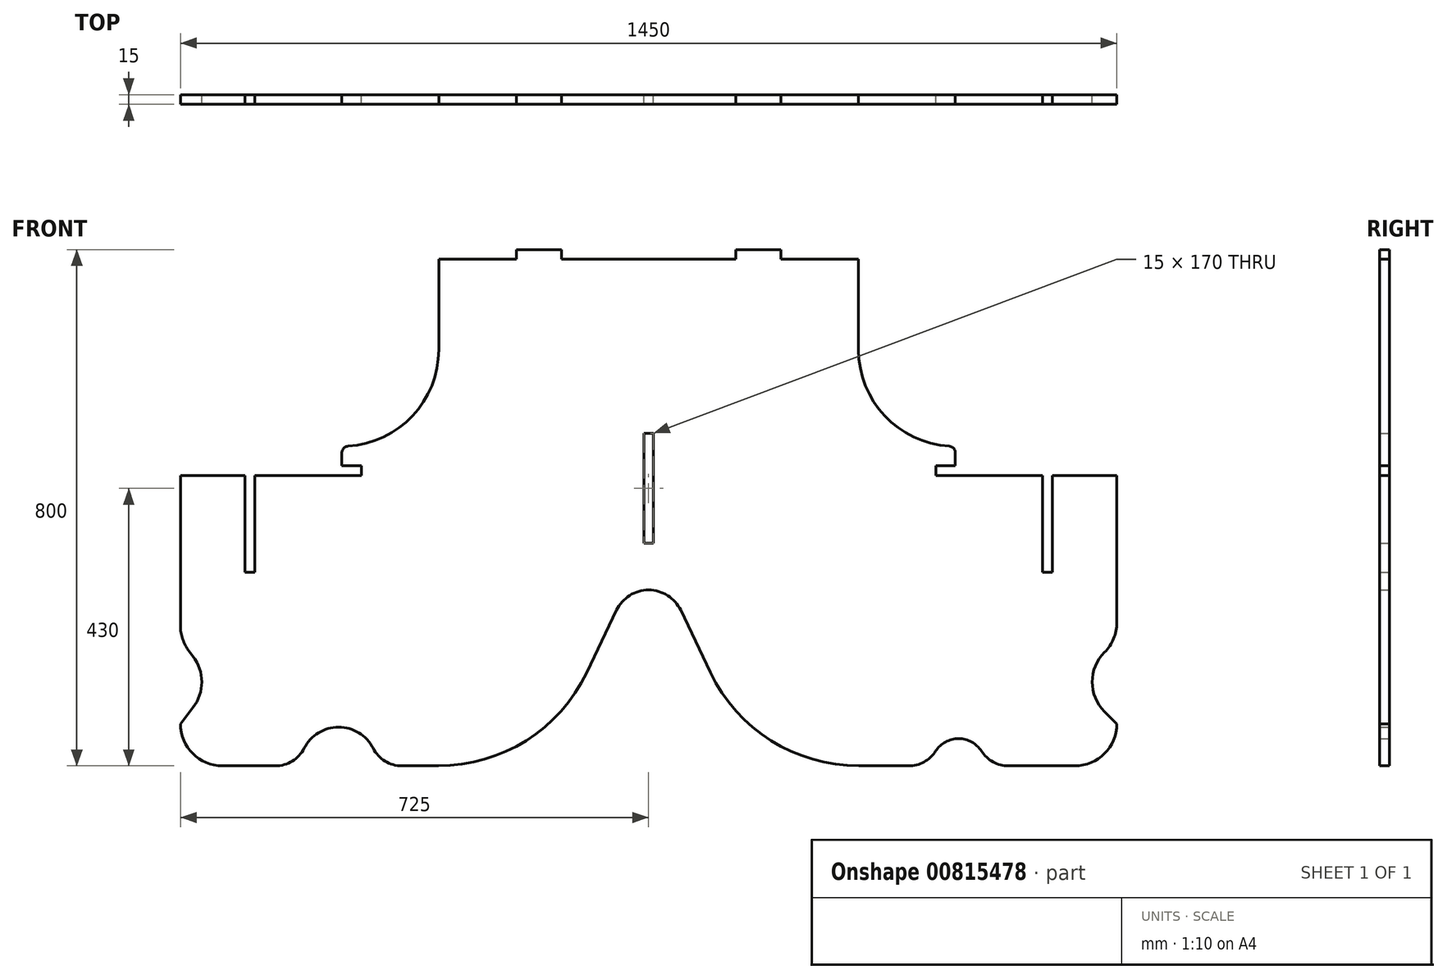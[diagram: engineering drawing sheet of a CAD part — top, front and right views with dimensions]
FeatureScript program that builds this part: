
annotation { "Feature Type Name" : "Feature", "Feature Type Description" : "" }
export const myFeature = defineFeature(function(context is Context, id is Id, definition is map)
    precondition{}
    {
        {
            var Q0;
            Q0=qCreatedBy(makeId("Front.planeOp"),FACE);
            var sketch = newSketch(context, id + "F0", { "sketchPlane" : qUnion([Q0])});
            skLineSegment(sketch, "E0.left", {"start": v(-325, 392.5) * mm, "end": v(-325, 312.5) * mm});
            skLineSegment(sketch, "E0.right", {"start": v(325, 392.5) * mm, "end": v(325, 312.5) * mm});
            skPoint(sketch, "E0.middle", {"position": v(0, 0) * mm});
            skLineSegment(sketch, "E1.bottom", {"start": v(-325, -392.5) * mm, "end": v(-382.02, -392.5) * mm});
            skLineSegment(sketch, "E2.bottom", {"start": v(325, -392.5) * mm, "end": v(402.54, -392.5) * mm});
            skLineSegment(sketch, "E3", {"start": v(-325, 392.5) * mm, "end": v(-205, 392.5) * mm});
            skLineSegment(sketch, "E4.top", {"start": v(-205, 407.5) * mm, "end": v(-135, 407.5) * mm});
            skLineSegment(sketch, "E4.left", {"start": v(-205, 392.5) * mm, "end": v(-205, 407.5) * mm});
            skLineSegment(sketch, "E4.right", {"start": v(-135, 392.5) * mm, "end": v(-135, 407.5) * mm});
            skLineSegment(sketch, "E5.top", {"start": v(205, 407.5) * mm, "end": v(135, 407.5) * mm});
            skLineSegment(sketch, "E5.left", {"start": v(205, 392.5) * mm, "end": v(205, 407.5) * mm});
            skLineSegment(sketch, "E5.right", {"start": v(135, 392.5) * mm, "end": v(135, 407.5) * mm});
            skLineSegment(sketch, "E6.trimOffspring", {"start": v(-135, 392.5) * mm, "end": v(135, 392.5) * mm});
            skLineSegment(sketch, "E7.trimOffspring", {"start": v(205, 392.5) * mm, "end": v(325, 392.5) * mm});
            skPoint(sketch, "E8.end.orphan", {"position": v(205, 374.36) * mm});
            skPoint(sketch, "E9.end.orphan", {"position": v(-205, 379.92) * mm});
            skLineSegment(sketch, "E10", {"start": v(0, -392.5) * mm, "end": v(0, -47.5) * mm});
            skLineSegment(sketch, "E11.right", {"start": v(-7.5, -47.5) * mm, "end": v(-7.5, 122.5) * mm});
            skLineSegment(sketch, "E12.MirrorCS", {"start": v(7.5, -47.5) * mm, "end": v(7.5, 122.5) * mm});
            skLineSegment(sketch, "E13", {"start": v(-7.5, 122.5) * mm, "end": v(7.5, 122.5) * mm});
            skLineSegment(sketch, "E14", {"start": v(-7.5, -47.5) * mm, "end": v(7.5, -47.5) * mm});
            skPoint(sketch, "E15.visualSharp", {"position": v(-146.32, -392.5) * mm});
            skPoint(sketch, "E16.visualSharp", {"position": v(165, -392.5) * mm});
            skLineSegment(sketch, "E17", {"start": v(-325.7, -392.5) * mm, "end": v(-325, -392.5) * mm});
            skLineSegment(sketch, "E18", {"start": v(325.7, -392.5) * mm, "end": v(325, -392.5) * mm});
            skLineSegment(sketch, "E19", {"start": v(-95.66, -247.52) * mm, "end": v(-49.62, -151.25) * mm});
            skLineSegment(sketch, "E20", {"start": v(49.62, -151.25) * mm, "end": v(95.66, -247.52) * mm});
            skPoint(sketch, "E21.visualSharp", {"position": v(0, -47.5) * mm});
            skArc(sketch, "E21.filletArc", {"start": v(49.62, -151.25) * mm, "mid": v(0, -119.98) * mm, "end": v(-49.62, -151.25) * mm});
            skPoint(sketch, "E22.visualSharp", {"position": v(-165, -392.5) * mm});
            skArc(sketch, "E22.filletArc", {"start": v(-325.7, -392.5) * mm, "mid": v(-189.75, -353.23) * mm, "end": v(-95.66, -247.52) * mm});
            skArc(sketch, "E23.filletArc", {"start": v(95.66, -247.52) * mm, "mid": v(189.75, -353.23) * mm, "end": v(325.7, -392.5) * mm});
            skLineSegment(sketch, "E24", {"start": v(-725, 57.5) * mm, "end": v(-625, 57.5) * mm});
            skLineSegment(sketch, "E25", {"start": v(-625, 57.5) * mm, "end": v(-625, -92.5) * mm});
            skLineSegment(sketch, "E26", {"start": v(-625, -92.5) * mm, "end": v(-610, -92.5) * mm});
            skLineSegment(sketch, "E27", {"start": v(-610, -92.5) * mm, "end": v(-610, 57.5) * mm});
            skLineSegment(sketch, "E28.trimOffspring", {"start": v(-625, 57.5) * mm, "end": v(-725, 57.5) * mm});
            skPoint(sketch, "E29.newPointA", {"position": v(-325, -392.5) * mm});
            skPoint(sketch, "E29.newPointB", {"position": v(-325, 57.5) * mm});
            skPoint(sketch, "E30.orphan", {"position": v(-525, 57.5) * mm});
            skPoint(sketch, "E31.newPointA", {"position": v(325, 57.5) * mm});
            skPoint(sketch, "E31.newPointB", {"position": v(325, -392.5) * mm});
            skLineSegment(sketch, "E32", {"start": v(725, 57.5) * mm, "end": v(625, 57.5) * mm});
            skLineSegment(sketch, "E33", {"start": v(625, 57.5) * mm, "end": v(625, -92.5) * mm});
            skLineSegment(sketch, "E34", {"start": v(625, -92.5) * mm, "end": v(610, -92.5) * mm});
            skLineSegment(sketch, "E35", {"start": v(610, -92.5) * mm, "end": v(610, 57.5) * mm});
            skLineSegment(sketch, "E36.trimOffspring", {"start": v(625, 57.5) * mm, "end": v(725, 57.5) * mm});
            skPoint(sketch, "E37.visualSharp", {"position": v(-725, -392.5) * mm});
            skArc(sketch, "E37.filletArc", {"start": v(-725, -327.5) * mm, "mid": v(-705.96, -373.46) * mm, "end": v(-660, -392.5) * mm});
            skPoint(sketch, "E38.visualSharp", {"position": v(725, -392.5) * mm});
            skArc(sketch, "E38.filletArc", {"start": v(660, -392.5) * mm, "mid": v(705.96, -373.46) * mm, "end": v(725, -327.5) * mm});
            skArc(sketch, "E39", {"start": v(515.45, -369.62) * mm, "mid": v(480, -350.3) * mm, "end": v(444.55, -369.62) * mm});
            skLineSegment(sketch, "E40.trimOffspring", {"start": v(557.46, -392.5) * mm, "end": v(660, -392.5) * mm});
            skPoint(sketch, "E41.visualSharp", {"position": v(437.8, -392.5) * mm});
            skArc(sketch, "E41.filletArc", {"start": v(402.54, -392.5) * mm, "mid": v(426.46, -386.4) * mm, "end": v(444.55, -369.62) * mm});
            skArc(sketch, "E42.filletArc", {"start": v(515.45, -369.62) * mm, "mid": v(533.54, -386.4) * mm, "end": v(557.46, -392.5) * mm});
            skArc(sketch, "E43", {"start": v(-426.56, -365.23) * mm, "mid": v(-480, -332.5) * mm, "end": v(-533.44, -365.23) * mm});
            skLineSegment(sketch, "E44.trimOffspring", {"start": v(-577.98, -392.5) * mm, "end": v(-660, -392.5) * mm});
            skPoint(sketch, "E45.visualSharp", {"position": v(-540, -392.5) * mm});
            skArc(sketch, "E45.filletArc", {"start": v(-577.98, -392.5) * mm, "mid": v(-551.87, -385.14) * mm, "end": v(-533.44, -365.23) * mm});
            skPoint(sketch, "E46.visualSharp", {"position": v(-420, -392.5) * mm});
            skArc(sketch, "E46.filletArc", {"start": v(-426.56, -365.23) * mm, "mid": v(-408.13, -385.14) * mm, "end": v(-382.02, -392.5) * mm});
            skLineSegment(sketch, "E47", {"start": v(525, 57.5) * mm, "end": v(525, 57.5) * mm});
            skLineSegment(sketch, "E48", {"start": v(325, 312.5) * mm, "end": v(325, 257.5) * mm});
            skLineSegment(sketch, "E49", {"start": v(-525, 57.5) * mm, "end": v(-525, 57.5) * mm});
            skLineSegment(sketch, "E50", {"start": v(-325, 312.5) * mm, "end": v(-325, 257.5) * mm});
            skLineSegment(sketch, "E51", {"start": v(-725, 57.5) * mm, "end": v(-725, -175.4) * mm});
            skLineSegment(sketch, "E52", {"start": v(-711.52, -215.02) * mm, "end": v(-705.49, -222.87) * mm});
            skLineSegment(sketch, "E53", {"start": v(-725, -327.5) * mm, "end": v(-705.49, -302.13) * mm});
            skPoint(sketch, "E54.visualSharp", {"position": v(-725, -197.5) * mm});
            skArc(sketch, "E54.filletArc", {"start": v(-725, -175.4) * mm, "mid": v(-721.54, -196.32) * mm, "end": v(-711.52, -215.02) * mm});
            skPoint(sketch, "E55.visualSharp", {"position": v(-675, -262.5) * mm});
            skArc(sketch, "E55.filletArc", {"start": v(-705.49, -302.13) * mm, "mid": v(-692, -262.5) * mm, "end": v(-705.49, -222.87) * mm});
            skLineSegment(sketch, "E56", {"start": v(705.96, -216.54) * mm, "end": v(705.96, -216.54) * mm});
            skLineSegment(sketch, "E57", {"start": v(705.96, -308.46) * mm, "end": v(725, -327.5) * mm});
            skLineSegment(sketch, "E58.trimOffspring", {"start": v(725, -170.58) * mm, "end": v(725, 57.5) * mm});
            skPoint(sketch, "E2.right.end.orphan", {"position": v(725, -262.5) * mm});
            skPoint(sketch, "E59.visualSharp", {"position": v(725, -197.5) * mm});
            skArc(sketch, "E59.filletArc", {"start": v(705.96, -216.54) * mm, "mid": v(720.05, -195.45) * mm, "end": v(725, -170.58) * mm});
            skPoint(sketch, "E60.visualSharp", {"position": v(660, -262.5) * mm});
            skArc(sketch, "E60.filletArc", {"start": v(705.96, -216.54) * mm, "mid": v(686.92, -262.5) * mm, "end": v(705.96, -308.46) * mm});
            skLineSegment(sketch, "E61", {"start": v(-610, 57.5) * mm, "end": v(-445, 57.5) * mm});
            skLineSegment(sketch, "E62", {"start": v(-445, 57.5) * mm, "end": v(-445, 72.5) * mm});
            skLineSegment(sketch, "E63", {"start": v(-445, 72.5) * mm, "end": v(-475, 72.5) * mm});
            skLineSegment(sketch, "E64", {"start": v(-475, 72.5) * mm, "end": v(-475, 92.81) * mm});
            skLineSegment(sketch, "E65", {"start": v(-475, 102.5) * mm, "end": v(-475, 102.5) * mm});
            skLineSegment(sketch, "E66", {"start": v(-325, 257.5) * mm, "end": v(-325, 252.5) * mm});
            skPoint(sketch, "E67.visualSharp", {"position": v(-325, 102.5) * mm});
            skArc(sketch, "E67.filletArc", {"start": v(-465.63, 102.8) * mm, "mid": v(-365.67, 149.8) * mm, "end": v(-325, 252.5) * mm});
            skPoint(sketch, "E68.visualSharp", {"position": v(-475, 102.5) * mm});
            skArc(sketch, "E68.filletArc", {"start": v(-465.63, 102.8) * mm, "mid": v(-472.29, 99.66) * mm, "end": v(-475, 92.81) * mm});
            skLineSegment(sketch, "E69", {"start": v(610, 57.5) * mm, "end": v(445, 57.5) * mm});
            skLineSegment(sketch, "E70", {"start": v(445, 57.5) * mm, "end": v(445, 72.5) * mm});
            skLineSegment(sketch, "E71", {"start": v(445, 72.5) * mm, "end": v(475, 72.5) * mm});
            skLineSegment(sketch, "E72", {"start": v(475, 72.5) * mm, "end": v(475, 92.81) * mm});
            skLineSegment(sketch, "E73", {"start": v(475, 102.5) * mm, "end": v(475, 102.5) * mm});
            skLineSegment(sketch, "E74", {"start": v(325, 252.5) * mm, "end": v(325, 257.5) * mm});
            skPoint(sketch, "E75.visualSharp", {"position": v(325, 102.5) * mm});
            skArc(sketch, "E75.filletArc", {"start": v(325, 252.5) * mm, "mid": v(365.67, 149.8) * mm, "end": v(465.63, 102.8) * mm});
            skPoint(sketch, "E76.visualSharp", {"position": v(475, 102.5) * mm});
            skArc(sketch, "E76.filletArc", {"start": v(475, 92.81) * mm, "mid": v(472.29, 99.66) * mm, "end": v(465.63, 102.8) * mm});
            skPoint(sketch, "E77.end.orphan", {"position": v(-770.64, -197.5) * mm});
            skPoint(sketch, "E78.end.orphan", {"position": v(-480, -417.73) * mm});
            skPoint(sketch, "E78.start.orphan", {"position": v(-660, -417.73) * mm});
            skPoint(sketch, "E79.end.orphan", {"position": v(-660, -442.96) * mm});
            skPoint(sketch, "E80.end.orphan", {"position": v(803.56, -197.5) * mm});
            skPoint(sketch, "E81.end.orphan", {"position": v(803.56, -262.5) * mm});
            skPoint(sketch, "E82.end.orphan", {"position": v(480, -424.92) * mm});
            skSolve(sketch);
        }
        {
            var Q0;
            Q0 = qSketchRegion(id + "F0", true);
            extrude(context, id + "F1", {"entities" : qUnion([Q0]), "depth" : 15 * mm, "offsetDistance" : 25 * mm});
        }
    });
